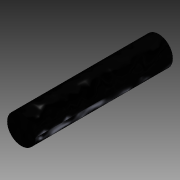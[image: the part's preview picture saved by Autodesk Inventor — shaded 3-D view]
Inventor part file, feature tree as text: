
AUTODESK INVENTOR PART (.ipt)
format: ipt  version: 2014 (Build 180170000, 170)  size: 69,120 bytes
history: native  units: in
note: dims shown in document units (in); Inventor stores cm internally (conversion verified against a paired STEP export)
features: extrude x1, sketch x1
ambient origin geometry x8: Origin, YZ Plane, XZ Plane, XY Plane, X Axis, Y Axis, Z Axis, Center Point
bodies: Solid1 (feature_tree)
feature tree (2):
  extrude  "Extrusion1"  Depth=3.0in TaperAngle=0.0deg
  sketch  "Sketch1"  dims[d0=0.62in d1=3.0in d2=0.0in]
